FCSTD DOCUMENT  (FreeCAD 1.0R39109 (Git))
Label: layout_32_mm
License: All rights reserved
LicenseURL: http://en.wikipedia.org/wiki/All_rights_reserved
objects: Sketcher::SketchObject×1, PartDesign::Body×1
note: 3 computed .brp shape members not serialized (recipe doc carries the construction recipe); baked Part::Feature solids carry a one-line shape summary decoded from their .brp

FEATURE [Sketcher::SketchObject] Sketch
  ArcFitTolerance = 1e-06
  AttachmentSupport = -> [XY_Plane]
  FullyConstrained = false
  MakeInternals = false
  MapMode = 5
  sketch-geometry (41):
    g0: LineSegment StartX=3 StartY=30 StartZ=0 EndX=3 EndY=15 EndZ=0
    g1: LineSegment StartX=3 StartY=15 StartZ=0 EndX=95 EndY=15 EndZ=0
    g2: LineSegment StartX=95 StartY=15 StartZ=0 EndX=95 EndY=30 EndZ=0
    g3: LineSegment StartX=95 StartY=30 StartZ=0 EndX=3 EndY=30 EndZ=0
    g4: LineSegment StartX=0 StartY=30 StartZ=0 EndX=-18 EndY=30 EndZ=0
    g5: LineSegment StartX=-18 StartY=30 StartZ=0 EndX=-18 EndY=0 EndZ=0
    g6: LineSegment StartX=-18 StartY=0 StartZ=0 EndX=0 EndY=0 EndZ=0
    g7: LineSegment StartX=0 StartY=0 StartZ=0 EndX=0 EndY=30 EndZ=0
    g8: LineSegment [constr] StartX=0 StartY=30 StartZ=0 EndX=3 EndY=30 EndZ=0
    g9: LineSegment [constr] StartX=9 StartY=15 StartZ=0 EndX=9 EndY=0 EndZ=0
    g10: LineSegment [constr] StartX=9 StartY=0 StartZ=0 EndX=89 EndY=0 EndZ=0
    g11: LineSegment [constr] StartX=89 StartY=0 StartZ=0 EndX=89 EndY=15 EndZ=0
    g12: LineSegment [constr] StartX=89 StartY=15 StartZ=0 EndX=9 EndY=15 EndZ=0
    g13: LineSegment [constr] StartX=0 StartY=7.5 StartZ=0 EndX=448 EndY=7.5 EndZ=0
    g14: Circle [constr] CenterX=32 CenterY=7.5 CenterZ=0 NormalX=0 NormalY=0 NormalZ=1 AngleXU=0 Radius=2
    g15: LineSegment StartX=98 StartY=30 StartZ=0 EndX=98 EndY=15 EndZ=0
    g16: LineSegment StartX=98 StartY=15 StartZ=0 EndX=190 EndY=15 EndZ=0
    g17: LineSegment StartX=190 StartY=15 StartZ=0 EndX=190 EndY=30 EndZ=0
    g18: LineSegment StartX=190 StartY=30 StartZ=0 EndX=98 EndY=30 EndZ=0
    g19: LineSegment [constr] StartX=95 StartY=30 StartZ=0 EndX=98 EndY=30 EndZ=0
    g20: Circle [constr] CenterX=64 CenterY=7.5 CenterZ=0 NormalX=0 NormalY=0 NormalZ=1 AngleXU=0 Radius=2
    g21: Circle [constr] CenterX=96 CenterY=7.5 CenterZ=0 NormalX=0 NormalY=0 NormalZ=1 AngleXU=0 Radius=1.71771
    g22: Circle [constr] CenterX=128 CenterY=7.5 CenterZ=0 NormalX=0 NormalY=0 NormalZ=1 AngleXU=0 Radius=2
    g23: Circle [constr] CenterX=192 CenterY=7.5 CenterZ=0 NormalX=0 NormalY=0 NormalZ=1 AngleXU=0 Radius=2
    g24: Circle [constr] CenterX=160 CenterY=7.5 CenterZ=0 NormalX=0 NormalY=0 NormalZ=1 AngleXU=0 Radius=2
    g25: LineSegment StartX=193 StartY=30 StartZ=0 EndX=193 EndY=15 EndZ=0
    g26: LineSegment StartX=193 StartY=15 StartZ=0 EndX=285 EndY=15 EndZ=0
    g27: LineSegment StartX=285 StartY=15 StartZ=0 EndX=285 EndY=30 EndZ=0
    g28: LineSegment StartX=285 StartY=30 StartZ=0 EndX=193 EndY=30 EndZ=0
    g29: LineSegment [constr] StartX=190 StartY=30 StartZ=0 EndX=193 EndY=30 EndZ=0
    g30: Circle [constr] CenterX=224 CenterY=7.5 CenterZ=0 NormalX=0 NormalY=0 NormalZ=1 AngleXU=0 Radius=2
    g31: Circle [constr] CenterX=256 CenterY=7.5 CenterZ=0 NormalX=0 NormalY=0 NormalZ=1 AngleXU=0 Radius=2
    g32: LineSegment StartX=288 StartY=30 StartZ=0 EndX=288 EndY=15 EndZ=0
    g33: LineSegment StartX=288 StartY=15 StartZ=0 EndX=380 EndY=15 EndZ=0
    g34: LineSegment StartX=380 StartY=15 StartZ=0 EndX=380 EndY=30 EndZ=0
    g35: LineSegment StartX=380 StartY=30 StartZ=0 EndX=288 EndY=30 EndZ=0
    g36: LineSegment [constr] StartX=285 StartY=30 StartZ=0 EndX=288 EndY=30 EndZ=0
    g37: Circle [constr] CenterX=288 CenterY=7.5 CenterZ=0 NormalX=0 NormalY=0 NormalZ=1 AngleXU=0 Radius=2
    g38: Circle [constr] CenterX=320 CenterY=7.5 CenterZ=0 NormalX=0 NormalY=0 NormalZ=1 AngleXU=0 Radius=2
    g39: Circle [constr] CenterX=352 CenterY=7.5 CenterZ=0 NormalX=0 NormalY=0 NormalZ=1 AngleXU=0 Radius=2
    g40: Circle [constr] CenterX=375.619 CenterY=7.5 CenterZ=0 NormalX=0 NormalY=0 NormalZ=1 AngleXU=0 Radius=2
  constraints (124):
    c: Coincident(g0,g1)
    c: Coincident(g1,g2)
    c: Coincident(g2,g3)
    c: Coincident(g3,g0)
    c: Vertical(g0)
    c: Vertical(g2)
    c: Horizontal(g1)
    c: Horizontal(g3)
    c: Coincident(g4,g5)
    c: Coincident(g5,g6)
    c: Coincident(g6,g7)
    c: Coincident(g7,g4)
    c: Horizontal(g4)
    c: Horizontal(g6)
    c: Vertical(g5)
    c: Vertical(g7)
    c: PointOnObject(g5,g-1)
    c: Coincident(g8,g4)
    c: Coincident(g8,g0)
    c: Horizontal(g8)
    c: DistanceY(g2,g2) = 15
    c: DistanceY(g5,g5) = 30
    c: Coincident(g9,g10)
    c: Coincident(g10,g11)
    c: Coincident(g11,g12)
    c: Coincident(g12,g9)
    c: Vertical(g9)
    c: Vertical(g11)
    c: Horizontal(g10)
    c: Horizontal(g12)
    c: PointOnObject(g9,g1)
    c: PointOnObject(g10,g-1)
    c: DistanceX(g10,g10) = 80
    c: Distance(g11,g1) = 6
    c: Distance(g9,g-2) = 9
    c: PointOnObject(g13,g-2)
    c: Horizontal(g13)
    c: Distance(g-1,g13) = 7.5
    c: PointOnObject(g14,g13)
    c: Diameter(g14) = 4
    c: DistanceX(g-1,g14) = 32
    c: Coincident(g15,g16)
    c: Coincident(g16,g17)
    c: Coincident(g17,g18)
    c: Coincident(g18,g15)
    c: Vertical(g15)
    c: Vertical(g17)
    c: Horizontal(g16)
    c: Horizontal(g18)
    c: Coincident(g19,g2)
    c: Coincident(g19,g15)
    c: Horizontal(g19)
    c: Equal(g2,g15)
    c: Equal(g3,g18)
    c: PointOnObject(g20,g13)
    c: Diameter(g20) = 4
    c: DistanceX(g14,g20) = 32
    c: PointOnObject(g21,g13)
    c: DistanceX(g20,g21) = 32
    c: PointOnObject(g22,g13)
    c: PointOnObject(g23,g13)
    c: PointOnObject(g24,g13)
    c: Equal(g20,g22)
    c: Equal(g20,g23)
    c: Equal(g20,g24)
    c: DistanceX(g21,g22) = 32
    c: Distance(g24,g22) = 32
    c: Distance(g23,g24) = 32
    c: Coincident(g25,g26)
    c: Coincident(g26,g27)
    c: Coincident(g27,g28)
    c: Coincident(g28,g25)
    c: Vertical(g25)
    c: Vertical(g27)
    c: Horizontal(g26)
    c: Horizontal(g28)
    c: Equal(g18,g28)
    c: Equal(g17,g25)
    c: Coincident(g29,g25)
    c: Horizontal(g29)
    c: Coincident(g29,g17)
    c: Equal(g19,g29)
    c: PointOnObject(g4,g-2)
    c: DistanceX(g4,g4) = 18
    c: Distance(g8,g8) = 3
    c: DistanceX(g3,g3) = 92
    c: Equal(g8,g19)
    c: DistanceX(g18,g18) = 92
    c: Distance(g19,g19) = 3
    c: Distance(g14,g0) = 29
    c: Distance(g22,g15) = 30
    c: Symmetric(g13,g13,g30)
    c: PointOnObject(g31,g13)
    c: Equal(g23,g30)
    c: Equal(g23,g31)
    c: DistanceX(g23,g30) = 32
    c: DistanceX(g30,g31) = 32
    c: Distance(g30,g25) = 31
    c: Coincident(g32,g33)
    c: Coincident(g33,g34)
    c: Coincident(g34,g35)
    c: Coincident(g35,g32)
    c: Vertical(g32)
    c: Vertical(g34)
    c: Horizontal(g33)
    c: Horizontal(g35)
    c: Equal(g27,g32)
    c: Equal(g28,g35)
    c: Coincident(g36,g27)
    c: Horizontal(g36)
    c: Coincident(g36,g32)
    c: Equal(g29,g36)
    c: PointOnObject(g37,g13)
    c: PointOnObject(g38,g13)
    c: PointOnObject(g39,g13)
    c: PointOnObject(g40,g13)
    c: Equal(g31,g37)
    c: Equal(g38,g31)
    c: Equal(g31,g39)
    c: Equal(g31,g40)
    c: Distance(g31,g37) = 32
    c: Distance(g37,g38) = 32
    c: Distance(g38,g39) = 32
    c: Distance(g38,g32) = 32
FEATURE [PartDesign::Body] Body
  AllowCompound = false
  Group = -> [Sketch]
  Origin = -> Origin
